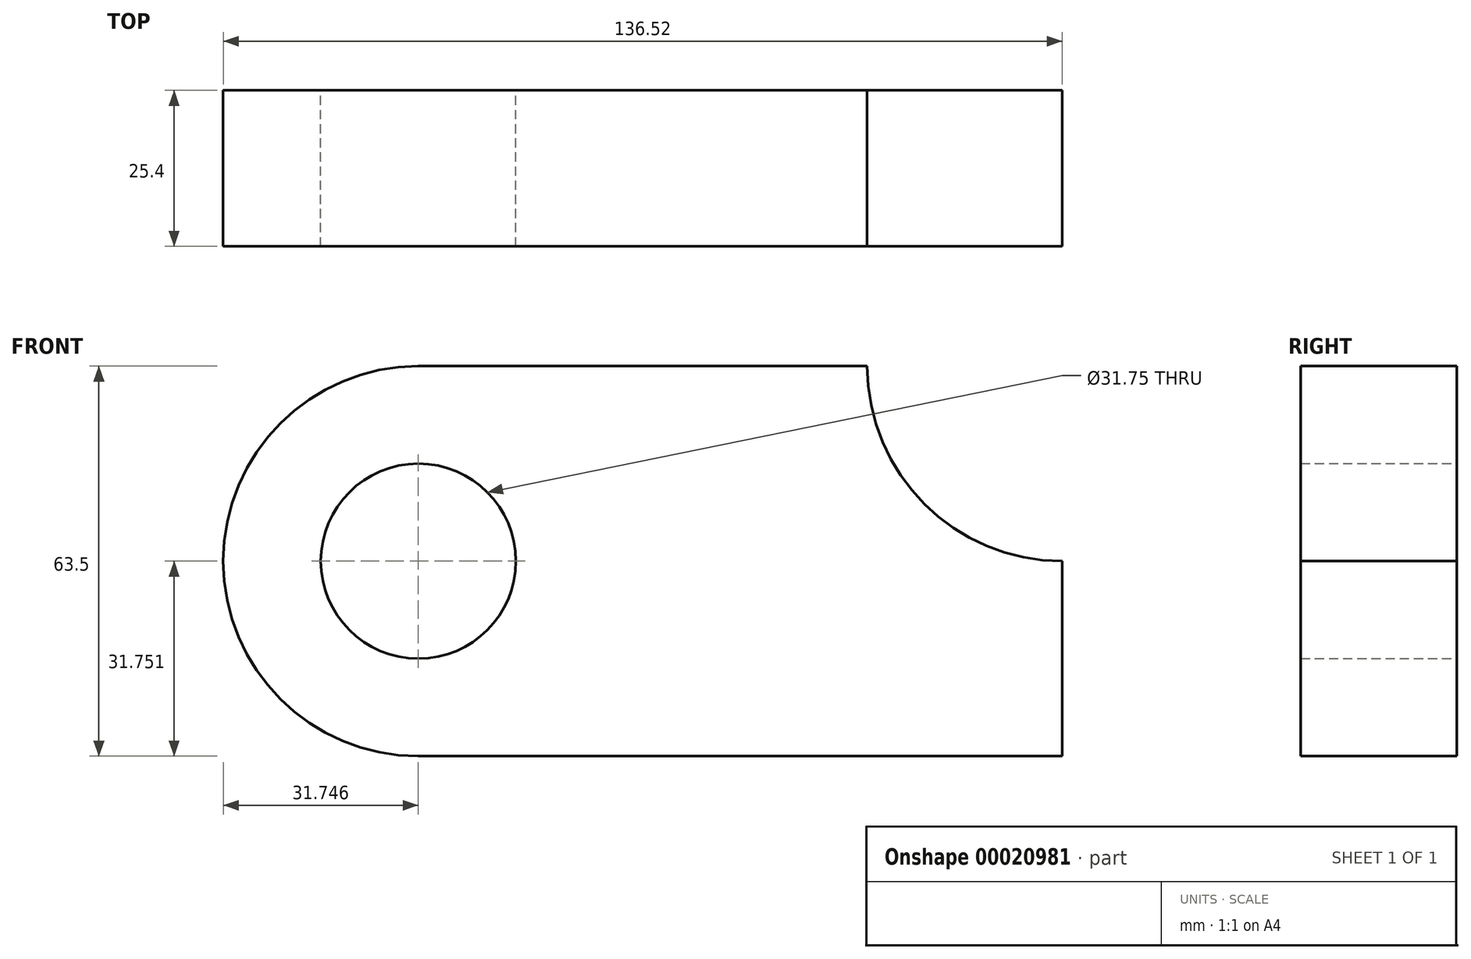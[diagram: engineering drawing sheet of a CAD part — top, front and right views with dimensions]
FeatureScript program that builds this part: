
annotation { "Feature Type Name" : "Feature", "Feature Type Description" : "" }
export const myFeature = defineFeature(function(context is Context, id is Id, definition is map)
    precondition{}
    {
        {
            var Q0;
            Q0=qCreatedBy(makeId("Front.planeOp"),FACE);
            var sketch = newSketch(context, id + "F0", { "sketchPlane" : qUnion([Q0])});
            skLineSegment(sketch, "E0.bottom", {"start": v(-42.61, 34.9) * mm, "end": v(30.41, 34.9) * mm});
            skLineSegment(sketch, "E0.top", {"start": v(-42.61, -28.6) * mm, "end": v(62.16, -28.6) * mm});
            skLineSegment(sketch, "E0.left", {"start": v(-42.61, 34.9) * mm, "end": v(-42.61, -28.6) * mm});
            skLineSegment(sketch, "E0.right", {"start": v(62.16, 3.15) * mm, "end": v(62.16, -28.6) * mm});
            skCircle(sketch, "E1", {"center": v(-42.61, 3.15) * mm, "radius": 15.88 * mm});
            skArc(sketch, "E2", {"start": v(30.41, 34.9) * mm, "mid": v(39.71, 12.45) * mm, "end": v(62.16, 3.15) * mm});
            skArc(sketch, "E3", {"start": v(-42.61, 34.9) * mm, "mid": v(-74.36, 3.15) * mm, "end": v(-42.61, -28.6) * mm});
            skSolve(sketch);
        }
        {
            var Q0;
            Q0 = qSketchRegion(id + "F0", true);
            extrude(context, id + "F1", {"entities" : qUnion([Q0]), "depth" : 25.4 * mm});
        }
    });
